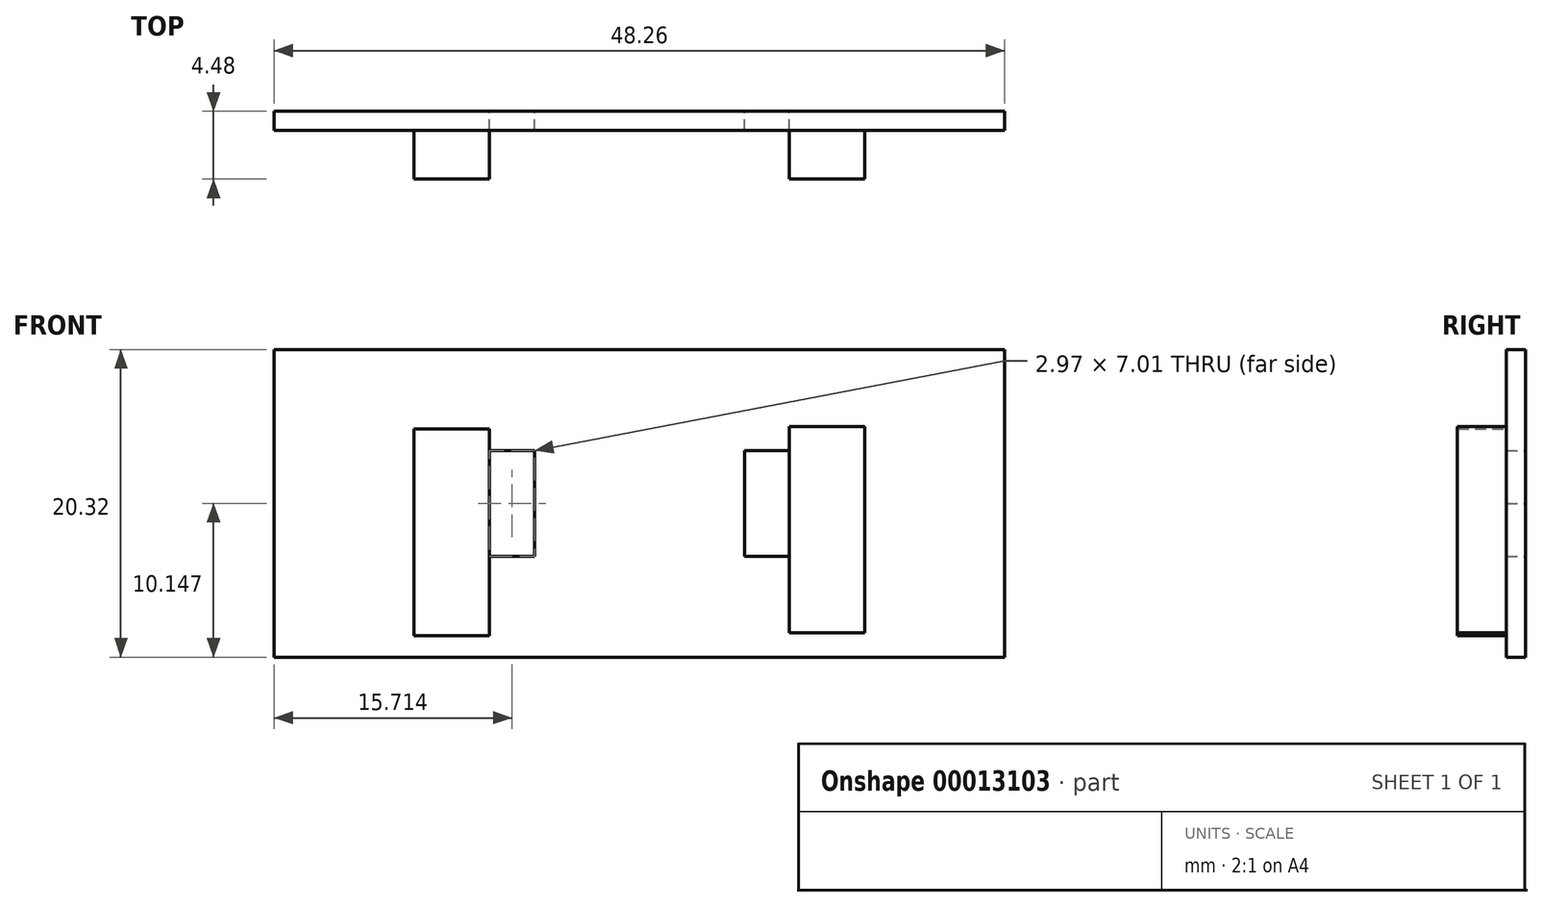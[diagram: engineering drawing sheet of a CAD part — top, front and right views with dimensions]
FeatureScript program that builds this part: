
annotation { "Feature Type Name" : "Feature", "Feature Type Description" : "" }
export const myFeature = defineFeature(function(context is Context, id is Id, definition is map)
    precondition{}
    {
        {
            var Q0;
            Q0=qCreatedBy(makeId("Front.planeOp"),FACE);
            var sketch = newSketch(context, id + "F0", { "sketchPlane" : qUnion([Q0])});
            skLineSegment(sketch, "E0.bottom", {"start": v(-24.7, 6.67) * mm, "end": v(23.55, 6.67) * mm});
            skLineSegment(sketch, "E0.top", {"start": v(-24.7, -13.65) * mm, "end": v(23.55, -13.65) * mm});
            skLineSegment(sketch, "E0.left", {"start": v(-24.7, 6.67) * mm, "end": v(-24.7, -13.65) * mm});
            skLineSegment(sketch, "E0.right", {"start": v(23.55, 6.67) * mm, "end": v(23.55, -13.65) * mm});
            skLineSegment(sketch, "E1", {"start": v(-24.7, -3.5) * mm, "end": v(-10.48, -3.5) * mm});
            skLineSegment(sketch, "E2", {"start": v(23.55, -3.5) * mm, "end": v(9.33, -3.5) * mm});
            skLineSegment(sketch, "E3.bottom", {"start": v(-10.48, -3.5) * mm, "end": v(-7.5, -3.5) * mm});
            skLineSegment(sketch, "E3.top", {"start": v(-10.48, 0) * mm, "end": v(-7.5, 0) * mm});
            skLineSegment(sketch, "E3.left", {"start": v(-10.48, -3.5) * mm, "end": v(-10.48, 0) * mm});
            skLineSegment(sketch, "E3.right", {"start": v(-7.5, -3.5) * mm, "end": v(-7.5, 0) * mm});
            skLineSegment(sketch, "E4.top", {"start": v(-10.48, -7) * mm, "end": v(-7.5, -7) * mm});
            skLineSegment(sketch, "E4.left", {"start": v(-10.48, -3.5) * mm, "end": v(-10.48, -7) * mm});
            skLineSegment(sketch, "E4.right", {"start": v(-7.5, -3.5) * mm, "end": v(-7.5, -7) * mm});
            skLineSegment(sketch, "E5.bottom", {"start": v(9.33, -3.5) * mm, "end": v(6.36, -3.5) * mm});
            skLineSegment(sketch, "E5.top", {"start": v(9.33, 0) * mm, "end": v(6.36, 0) * mm});
            skLineSegment(sketch, "E5.left", {"start": v(9.33, -3.5) * mm, "end": v(9.33, 0) * mm});
            skLineSegment(sketch, "E5.right", {"start": v(6.36, -3.5) * mm, "end": v(6.36, 0) * mm});
            skLineSegment(sketch, "E6.bottom", {"start": v(6.36, -3.5) * mm, "end": v(9.33, -3.5) * mm});
            skLineSegment(sketch, "E6.top", {"start": v(6.36, -7) * mm, "end": v(9.33, -7) * mm});
            skLineSegment(sketch, "E6.left", {"start": v(6.36, -3.5) * mm, "end": v(6.36, -7) * mm});
            skLineSegment(sketch, "E6.right", {"start": v(9.33, -3.5) * mm, "end": v(9.33, -7) * mm});
            skSolve(sketch);
        }
        {
            var Q0;
            {var subQ3=sQuery(id+"F0.wireOp",EDGE,"E0.bottom");Q0=makeQuery(id+"F0.imprint","IMPRINT",FACE,{"disambiguationData":[TD([[makeQuery(id+"F0.imprint","IMPRINT",EDGE,{"derivedFrom":subQ3}),-1.0]])]});}
            extrude(context, id + "F1", {"entities" : qUnion([Q0]), "depth" : 1.27 * mm});
        }
        {
            var Q0;
            Q0=makeQuery(id+"F1.opExtrude","CAP_FACE",FACE,{"disambiguationData":[OSD([sQuery(id+"F0.wireOp",EDGE,"E0.bottom"),sQuery(id+"F0.wireOp",EDGE,"E0.top"),sQuery(id+"F0.wireOp",EDGE,"E0.left"),sQuery(id+"F0.wireOp",EDGE,"E0.right"),sQuery(id+"F0.wireOp",EDGE,"E3.top"),sQuery(id+"F0.wireOp",EDGE,"E3.left"),sQuery(id+"F0.wireOp",EDGE,"E3.right"),sQuery(id+"F0.wireOp",EDGE,"E4.top"),sQuery(id+"F0.wireOp",EDGE,"E4.left"),sQuery(id+"F0.wireOp",EDGE,"E4.right"),sQuery(id+"F0.wireOp",EDGE,"E5.bottom"),sQuery(id+"F0.wireOp",EDGE,"E5.top"),sQuery(id+"F0.wireOp",EDGE,"E5.left"),sQuery(id+"F0.wireOp",EDGE,"E5.right"),sQuery(id+"F0.wireOp",EDGE,"E6.top"),sQuery(id+"F0.wireOp",EDGE,"E6.left"),sQuery(id+"F0.wireOp",EDGE,"E6.right")])],"isStart":false});
            var sketch = newSketch(context, id + "F2", { "sketchPlane" : qUnion([Q0])});
            skLineSegment(sketch, "E7.bottom", {"start": v(9.33, 1.6) * mm, "end": v(14.3, 1.6) * mm});
            skLineSegment(sketch, "E7.top", {"start": v(9.33, -12.05) * mm, "end": v(14.3, -12.05) * mm});
            skLineSegment(sketch, "E7.left", {"start": v(9.33, 1.6) * mm, "end": v(9.33, -12.05) * mm});
            skLineSegment(sketch, "E7.right", {"start": v(14.3, 1.6) * mm, "end": v(14.3, -12.05) * mm});
            skLineSegment(sketch, "E8.bottom", {"start": v(-10.5, 1.42) * mm, "end": v(-15.47, 1.42) * mm});
            skLineSegment(sketch, "E8.top", {"start": v(-10.5, -12.22) * mm, "end": v(-15.47, -12.22) * mm});
            skLineSegment(sketch, "E8.left", {"start": v(-10.5, 1.42) * mm, "end": v(-10.5, -12.22) * mm});
            skLineSegment(sketch, "E8.right", {"start": v(-15.47, 1.42) * mm, "end": v(-15.47, -12.22) * mm});
            skSolve(sketch);
        }
        {
            var Q0;
            Q0=makeQuery(id+"F2.imprint","IMPRINT",FACE,{"disambiguationData":[TD([[makeQuery(id+"F2.imprint","IMPRINT",EDGE,{"derivedFrom":sQuery(id+"F2.wireOp",EDGE,"E8.bottom")}),1.0]])]});
            var Q1;
            {var subQ4=sQuery(id+"F2.wireOp",EDGE,"E7.bottom");Q1=makeQuery(id+"F2.imprint","IMPRINT",FACE,{"disambiguationData":[TD([[makeQuery(id+"F2.imprint","IMPRINT",EDGE,{"derivedFrom":subQ4}),-1.0]])]});}
            extrude(context, id + "F3", {"entities" : qUnion([Q0, Q1]), "operationType" : NewBodyOperationType.ADD, "depth" : 3.2 * mm});
        }
    });
